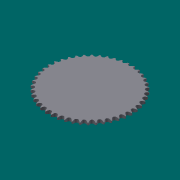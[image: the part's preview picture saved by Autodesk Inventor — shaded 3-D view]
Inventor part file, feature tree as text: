
AUTODESK INVENTOR PART (.ipt)
format: ipt  version: 2016 (Build 200138000, 138)  size: 906,240 bytes
history: native  units: mm
features: other x6, extrude x2, pattern_linear x1, pattern_circular x1
ambient origin geometry x8: Origin, YZ Plane, XZ Plane, XY Plane, X Axis, Y Axis, Z Axis, Center Point
bodies: Solid1 (feature_tree)
feature tree (10):
  other  "Theoretical Tooth Profile"
  other  "Tooth Profile"
  other  "Section Profile"
  other  "Shroud"
  other  "Strand"
  pattern_linear  "Strand Pattern"  Spacing1=186.101273mm  [1 undecoded]
  extrude  "Theoretical Tooth"  Depth=1.36591mm
  extrude  "Tooth"  Depth=3.91375mm
  pattern_circular  "Tooth Pattern"  [2 undecoded]
  other  "Timing Plane"
note: 3 required parameter values undecoded (feature->parameter linkage not recoverable at this tier; creation-order binding heuristic only, values carry confidence <= 0.55)
